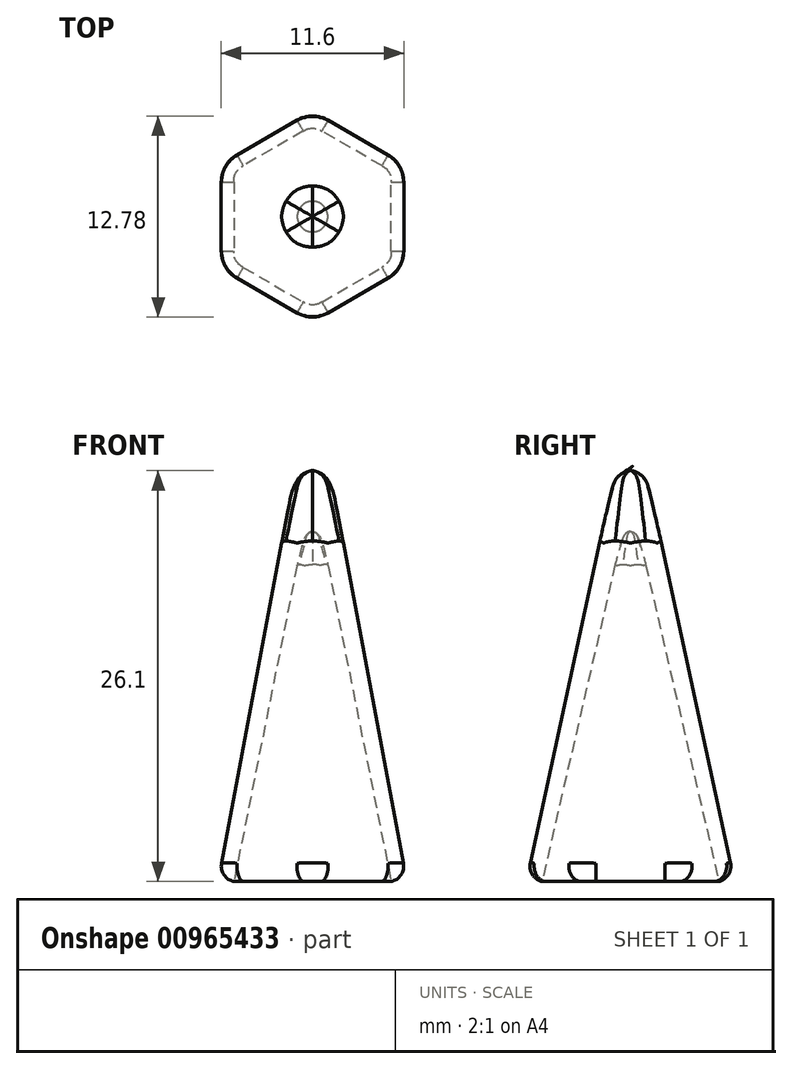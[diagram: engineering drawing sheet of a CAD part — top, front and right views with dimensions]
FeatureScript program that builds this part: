
annotation { "Feature Type Name" : "Feature", "Feature Type Description" : "" }
export const myFeature = defineFeature(function(context is Context, id is Id, definition is map)
    precondition{}
    {
        {
            var Q0;
            Q0=qCreatedBy(makeId("Top.planeOp"),FACE);
            var sketch = newSketch(context, id + "F0", { "sketchPlane" : qUnion([Q0])});
            skPoint(sketch, "E0", {"position": v(0, 5.77) * mm});
            skPoint(sketch, "E1.1.0", {"position": v(-5, 2.89) * mm});
            skPoint(sketch, "E1.2.0", {"position": v(-5, -2.89) * mm});
            skPoint(sketch, "E1.3.0", {"position": v(0, -5.77) * mm});
            skPoint(sketch, "E1.4.0", {"position": v(5, -2.89) * mm});
            skPoint(sketch, "E1.5.0", {"position": v(5, 2.89) * mm});
            skPoint(sketch, "E1.center", {"position": v(0, 0) * mm});
            skLineSegment(sketch, "E2", {"start": v(0, 5.77) * mm, "end": v(5, 2.89) * mm});
            skLineSegment(sketch, "E3", {"start": v(5, -2.89) * mm, "end": v(0, -5.77) * mm});
            skLineSegment(sketch, "E4", {"start": v(-5, -2.89) * mm, "end": v(-5, 2.89) * mm});
            skLineSegment(sketch, "E5", {"start": v(-5, 2.89) * mm, "end": v(0, 5.77) * mm});
            skLineSegment(sketch, "E6", {"start": v(5, 2.89) * mm, "end": v(5, -2.89) * mm});
            skLineSegment(sketch, "E7", {"start": v(0, -5.77) * mm, "end": v(-5, -2.89) * mm});
            skLineSegment(sketch, "E8.0", {"start": v(0, -6.93) * mm, "end": v(-6, -3.46) * mm});
            skLineSegment(sketch, "E8.1", {"start": v(-6, 3.46) * mm, "end": v(0, 6.93) * mm});
            skLineSegment(sketch, "E8.2", {"start": v(0, 6.93) * mm, "end": v(6, 3.46) * mm});
            skLineSegment(sketch, "E8.3", {"start": v(-6, -3.46) * mm, "end": v(-6, 3.46) * mm});
            skLineSegment(sketch, "E8.4", {"start": v(6, 3.46) * mm, "end": v(6, -3.46) * mm});
            skLineSegment(sketch, "E8.5", {"start": v(6, -3.46) * mm, "end": v(0, -6.93) * mm});
            skSolve(sketch);
        }
        {
            var Q0;
            Q0=qCreatedBy(makeId("Top.planeOp"),FACE);
            cPlane(context, id + "F1", {"entities" : qUnion([Q0]), "cplaneType" : CPlaneType.OFFSET, "offset" : 25 * mm, "width" : 150 * mm, "height" : 150 * mm});
        }
        {
            var Q0;
            Q0=qCreatedBy(id+"F1.planeOp",FACE);
            var sketch = newSketch(context, id + "F2", { "sketchPlane" : qUnion([Q0])});
            skPoint(sketch, "E9", {"position": v(0, 0) * mm});
            skSolve(sketch);
        }
        {
            var Q0;
            Q0=qCreatedBy(makeId("Top.planeOp"),FACE);
            cPlane(context, id + "F3", {"entities" : qUnion([Q0]), "cplaneType" : CPlaneType.OFFSET, "offset" : 32 * mm, "width" : 150 * mm, "height" : 150 * mm});
        }
        {
            var Q0;
            Q0=qCreatedBy(id+"F3.planeOp",FACE);
            var sketch = newSketch(context, id + "F4", { "sketchPlane" : qUnion([Q0])});
            skPoint(sketch, "E10", {"position": v(0, 0) * mm});
            skSolve(sketch);
        }
        {
            var Q0;
            Q0=qCreatedBy(makeId("Top.planeOp"),FACE);
            var sketch = newSketch(context, id + "F5", { "sketchPlane" : qUnion([Q0])});
            skPoint(sketch, "E11", {"position": v(0, 6.93) * mm});
            skPoint(sketch, "E12.1.0", {"position": v(-6, 3.46) * mm});
            skPoint(sketch, "E12.2.0", {"position": v(-6, -3.46) * mm});
            skPoint(sketch, "E12.3.0", {"position": v(0, -6.93) * mm});
            skPoint(sketch, "E12.4.0", {"position": v(6, -3.46) * mm});
            skPoint(sketch, "E12.5.0", {"position": v(6, 3.46) * mm});
            skPoint(sketch, "E12.center", {"position": v(0, 0) * mm});
            skLineSegment(sketch, "E13", {"start": v(-6, 3.46) * mm, "end": v(0, 6.93) * mm});
            skLineSegment(sketch, "E14", {"start": v(0, 6.93) * mm, "end": v(6, 3.46) * mm});
            skLineSegment(sketch, "E15", {"start": v(6, 3.46) * mm, "end": v(6, -3.46) * mm});
            skLineSegment(sketch, "E16", {"start": v(6, -3.46) * mm, "end": v(0, -6.93) * mm});
            skLineSegment(sketch, "E17", {"start": v(0, -6.93) * mm, "end": v(-6, -3.46) * mm});
            skLineSegment(sketch, "E18", {"start": v(-6, -3.46) * mm, "end": v(-6, 3.46) * mm});
            skSolve(sketch);
        }
        {
            var Q0;
            Q0=makeQuery(id+"F5.imprint","IMPRINT",FACE,{"disambiguationData":[TD([[makeQuery(id+"F5.imprint","IMPRINT",EDGE,{"derivedFrom":sQuery(id+"F5.wireOp",EDGE,"E13")}),-1.0]])]});
            var Q1;
            Q1=sQuery(id+"F4.wireOp",VERTEX,"E10");
            loft(context, id + "F6", {"sheetProfilesArray" : [{ "sheetProfileEntities" : qUnion([Q0]) }, { "sheetProfileEntities" : qUnion([Q1]) }]});
        }
        {
            var Q1;
            Q1=makeQuery(id+"F0.imprint","IMPRINT",FACE,{"disambiguationData":[TD([[makeQuery(id+"F0.imprint","IMPRINT",EDGE,{"derivedFrom":sQuery(id+"F0.wireOp",EDGE,"E2")}),-1.0]])]});
            var Q2;
            Q2=sQuery(id+"F2.wireOp",VERTEX,"E9");
            loft(context, id + "F7", {"operationType" : NewBodyOperationType.REMOVE, "sheetProfilesArray" : [{ "sheetProfileEntities" : qUnion([Q1]) }, { "sheetProfileEntities" : qUnion([Q2]) }]});
        }
        {
            var Q0;
            Q0=makeQuery(id+"F6.opLoft","SWEPT_EDGE",EDGE,{"disambiguationData":[OSD([sQuery(id+"F4.wireOp",VERTEX,"E10"),sQuery(id+"F5.wireOp",EDGE,"E14"),sQuery(id+"F5.wireOp",EDGE,"E15")])]});
            var Q1;
            Q1=makeQuery(id+"F6.opLoft","SWEPT_EDGE",EDGE,{"disambiguationData":[OSD([sQuery(id+"F4.wireOp",VERTEX,"E10"),sQuery(id+"F5.wireOp",EDGE,"E15"),sQuery(id+"F5.wireOp",EDGE,"E16")])]});
            var Q2;
            Q2=makeQuery(id+"F6.opLoft","SWEPT_EDGE",EDGE,{"disambiguationData":[OSD([sQuery(id+"F4.wireOp",VERTEX,"E10"),sQuery(id+"F5.wireOp",EDGE,"E16"),sQuery(id+"F5.wireOp",EDGE,"E17")])]});
            var Q3;
            Q3=makeQuery(id+"F6.opLoft","SWEPT_EDGE",EDGE,{"disambiguationData":[OSD([sQuery(id+"F4.wireOp",VERTEX,"E10"),sQuery(id+"F5.wireOp",EDGE,"E17"),sQuery(id+"F5.wireOp",EDGE,"E18")])]});
            var Q4;
            Q4=makeQuery(id+"F6.opLoft","SWEPT_EDGE",EDGE,{"disambiguationData":[OSD([sQuery(id+"F4.wireOp",VERTEX,"E10"),sQuery(id+"F5.wireOp",EDGE,"E13"),sQuery(id+"F5.wireOp",EDGE,"E18")])]});
            var Q5;
            Q5=makeQuery(id+"F6.opLoft","SWEPT_EDGE",EDGE,{"disambiguationData":[OSD([sQuery(id+"F4.wireOp",VERTEX,"E10"),sQuery(id+"F5.wireOp",EDGE,"E13"),sQuery(id+"F5.wireOp",EDGE,"E14")])]});
            fillet(context, id + "F8", {"entities" : qUnion([Q0, Q1, Q2, Q3, Q4, Q5]), "radius" : 2 * mm, "tangentPropagation" : true, "allowEdgeOverflow" : false});
        }
        {
            var Q0;
            Q0=makeQuery(id+"F7.boolean.opBoolean","COPY",EDGE,{"derivedFrom":makeQuery(id+"F7.opLoft","SWEPT_EDGE",EDGE,{"disambiguationData":[OSD([sQuery(id+"F0.wireOp",EDGE,"E4"),sQuery(id+"F0.wireOp",EDGE,"E7"),sQuery(id+"F2.wireOp",VERTEX,"E9")])]})});
            var Q1;
            Q1=makeQuery(id+"F7.boolean.opBoolean","COPY",EDGE,{"derivedFrom":makeQuery(id+"F7.opLoft","SWEPT_EDGE",EDGE,{"disambiguationData":[OSD([sQuery(id+"F0.wireOp",EDGE,"E3"),sQuery(id+"F0.wireOp",EDGE,"E7"),sQuery(id+"F2.wireOp",VERTEX,"E9")])]})});
            var Q2;
            Q2=makeQuery(id+"F7.boolean.opBoolean","COPY",EDGE,{"derivedFrom":makeQuery(id+"F7.opLoft","SWEPT_EDGE",EDGE,{"disambiguationData":[OSD([sQuery(id+"F0.wireOp",EDGE,"E3"),sQuery(id+"F0.wireOp",EDGE,"E6"),sQuery(id+"F2.wireOp",VERTEX,"E9")])]})});
            var Q3;
            Q3=makeQuery(id+"F7.boolean.opBoolean","COPY",EDGE,{"derivedFrom":makeQuery(id+"F7.opLoft","SWEPT_EDGE",EDGE,{"disambiguationData":[OSD([sQuery(id+"F0.wireOp",EDGE,"E2"),sQuery(id+"F0.wireOp",EDGE,"E6"),sQuery(id+"F2.wireOp",VERTEX,"E9")])]})});
            var Q4;
            Q4=makeQuery(id+"F7.boolean.opBoolean","COPY",EDGE,{"derivedFrom":makeQuery(id+"F7.opLoft","SWEPT_EDGE",EDGE,{"disambiguationData":[OSD([sQuery(id+"F0.wireOp",EDGE,"E2"),sQuery(id+"F0.wireOp",EDGE,"E5"),sQuery(id+"F2.wireOp",VERTEX,"E9")])]})});
            var Q5;
            Q5=makeQuery(id+"F7.boolean.opBoolean","COPY",EDGE,{"derivedFrom":makeQuery(id+"F7.opLoft","SWEPT_EDGE",EDGE,{"disambiguationData":[OSD([sQuery(id+"F0.wireOp",EDGE,"E4"),sQuery(id+"F0.wireOp",EDGE,"E5"),sQuery(id+"F2.wireOp",VERTEX,"E9")])]})});
            fillet(context, id + "F9", {"entities" : qUnion([Q0, Q1, Q2, Q3, Q4, Q5]), "radius" : 1 * mm, "tangentPropagation" : true, "allowEdgeOverflow" : false});
        }
        {
            var Q0;
            Q0=makeQuery(id+"F6.opLoft","MID_CAP_EDGE",EDGE,{"disambiguationData":[OSD([sQuery(id+"F5.wireOp",EDGE,"E16"),sQuery(id+"F5.wireOp",EDGE,"E17"),sQuery(id+"F5.wireOp",EDGE,"E18")])],"capPos":0.0});
            var Q1;
            {var subQ0=sQuery(id+"F5.wireOp",EDGE,"E16");var subQ1=sQuery(id+"F5.wireOp",EDGE,"E17");Q1=makeQuery(id+"F8.opFillet","BLEND_EDGE",EDGE,{"blendedFrom":[makeQuery(id+"F6.opLoft","SWEPT_EDGE",EDGE,{"disambiguationData":[OSD([sQuery(id+"F4.wireOp",VERTEX,"E10"),subQ0,subQ1])]}),makeQuery(id+"F6.opLoft","CAP_FACE",FACE,{"disambiguationData":[OSD([makeQuery(id+"F5.imprint","IMPRINT",FACE,{"disambiguationData":[TD([[makeQuery(id+"F5.imprint","IMPRINT",EDGE,{"derivedFrom":sQuery(id+"F5.wireOp",EDGE,"E13")}),-1.0]])]})])],"isStart":true})],"blendedInto":[makeQuery(id+"F6.opLoft","CAP_FACE",FACE,{"disambiguationData":[OSD([makeQuery(id+"F5.imprint","IMPRINT",FACE,{"disambiguationData":[TD([[makeQuery(id+"F5.imprint","IMPRINT",EDGE,{"derivedFrom":sQuery(id+"F5.wireOp",EDGE,"E13")}),-1.0]])]})])],"isStart":true})]});}
            var Q2;
            Q2=makeQuery(id+"F6.opLoft","MID_CAP_EDGE",EDGE,{"disambiguationData":[OSD([sQuery(id+"F5.wireOp",EDGE,"E15"),sQuery(id+"F5.wireOp",EDGE,"E16"),sQuery(id+"F5.wireOp",EDGE,"E17")])],"capPos":0.0});
            var Q3;
            {var subQ0=sQuery(id+"F5.wireOp",EDGE,"E16");var subQ1=sQuery(id+"F5.wireOp",EDGE,"E15");Q3=makeQuery(id+"F8.opFillet","BLEND_EDGE",EDGE,{"blendedFrom":[makeQuery(id+"F6.opLoft","SWEPT_EDGE",EDGE,{"disambiguationData":[OSD([sQuery(id+"F4.wireOp",VERTEX,"E10"),subQ1,subQ0])]}),makeQuery(id+"F6.opLoft","CAP_FACE",FACE,{"disambiguationData":[OSD([makeQuery(id+"F5.imprint","IMPRINT",FACE,{"disambiguationData":[TD([[makeQuery(id+"F5.imprint","IMPRINT",EDGE,{"derivedFrom":sQuery(id+"F5.wireOp",EDGE,"E13")}),-1.0]])]})])],"isStart":true})],"blendedInto":[makeQuery(id+"F6.opLoft","CAP_FACE",FACE,{"disambiguationData":[OSD([makeQuery(id+"F5.imprint","IMPRINT",FACE,{"disambiguationData":[TD([[makeQuery(id+"F5.imprint","IMPRINT",EDGE,{"derivedFrom":sQuery(id+"F5.wireOp",EDGE,"E13")}),-1.0]])]})])],"isStart":true})]});}
            var Q4;
            Q4=makeQuery(id+"F6.opLoft","MID_CAP_EDGE",EDGE,{"disambiguationData":[OSD([sQuery(id+"F5.wireOp",EDGE,"E14"),sQuery(id+"F5.wireOp",EDGE,"E15"),sQuery(id+"F5.wireOp",EDGE,"E16")])],"capPos":0.0});
            var Q5;
            {var subQ0=sQuery(id+"F5.wireOp",EDGE,"E15");var subQ1=sQuery(id+"F5.wireOp",EDGE,"E14");Q5=makeQuery(id+"F8.opFillet","BLEND_EDGE",EDGE,{"blendedFrom":[makeQuery(id+"F6.opLoft","SWEPT_EDGE",EDGE,{"disambiguationData":[OSD([sQuery(id+"F4.wireOp",VERTEX,"E10"),subQ1,subQ0])]}),makeQuery(id+"F6.opLoft","CAP_FACE",FACE,{"disambiguationData":[OSD([makeQuery(id+"F5.imprint","IMPRINT",FACE,{"disambiguationData":[TD([[makeQuery(id+"F5.imprint","IMPRINT",EDGE,{"derivedFrom":sQuery(id+"F5.wireOp",EDGE,"E13")}),-1.0]])]})])],"isStart":true})],"blendedInto":[makeQuery(id+"F6.opLoft","CAP_FACE",FACE,{"disambiguationData":[OSD([makeQuery(id+"F5.imprint","IMPRINT",FACE,{"disambiguationData":[TD([[makeQuery(id+"F5.imprint","IMPRINT",EDGE,{"derivedFrom":sQuery(id+"F5.wireOp",EDGE,"E13")}),-1.0]])]})])],"isStart":true})]});}
            var Q6;
            Q6=makeQuery(id+"F6.opLoft","MID_CAP_EDGE",EDGE,{"disambiguationData":[OSD([sQuery(id+"F5.wireOp",EDGE,"E13"),sQuery(id+"F5.wireOp",EDGE,"E14"),sQuery(id+"F5.wireOp",EDGE,"E15")])],"capPos":0.0});
            var Q7;
            {var subQ0=sQuery(id+"F5.wireOp",EDGE,"E14");var subQ1=sQuery(id+"F5.wireOp",EDGE,"E13");Q7=makeQuery(id+"F8.opFillet","BLEND_EDGE",EDGE,{"blendedFrom":[makeQuery(id+"F6.opLoft","SWEPT_EDGE",EDGE,{"disambiguationData":[OSD([sQuery(id+"F4.wireOp",VERTEX,"E10"),subQ1,subQ0])]}),makeQuery(id+"F6.opLoft","CAP_FACE",FACE,{"disambiguationData":[OSD([makeQuery(id+"F5.imprint","IMPRINT",FACE,{"disambiguationData":[TD([[makeQuery(id+"F5.imprint","IMPRINT",EDGE,{"derivedFrom":subQ1}),-1.0]])]})])],"isStart":true})],"blendedInto":[makeQuery(id+"F6.opLoft","CAP_FACE",FACE,{"disambiguationData":[OSD([makeQuery(id+"F5.imprint","IMPRINT",FACE,{"disambiguationData":[TD([[makeQuery(id+"F5.imprint","IMPRINT",EDGE,{"derivedFrom":subQ1}),-1.0]])]})])],"isStart":true})]});}
            var Q8;
            Q8=makeQuery(id+"F6.opLoft","MID_CAP_EDGE",EDGE,{"disambiguationData":[OSD([sQuery(id+"F5.wireOp",EDGE,"E13"),sQuery(id+"F5.wireOp",EDGE,"E14"),sQuery(id+"F5.wireOp",EDGE,"E18")])],"capPos":0.0});
            var Q9;
            {var subQ0=sQuery(id+"F5.wireOp",EDGE,"E13");var subQ1=sQuery(id+"F5.wireOp",EDGE,"E18");Q9=makeQuery(id+"F8.opFillet","BLEND_EDGE",EDGE,{"blendedFrom":[makeQuery(id+"F6.opLoft","SWEPT_EDGE",EDGE,{"disambiguationData":[OSD([sQuery(id+"F4.wireOp",VERTEX,"E10"),subQ0,subQ1])]}),makeQuery(id+"F6.opLoft","CAP_FACE",FACE,{"disambiguationData":[OSD([makeQuery(id+"F5.imprint","IMPRINT",FACE,{"disambiguationData":[TD([[makeQuery(id+"F5.imprint","IMPRINT",EDGE,{"derivedFrom":subQ0}),-1.0]])]})])],"isStart":true})],"blendedInto":[makeQuery(id+"F6.opLoft","CAP_FACE",FACE,{"disambiguationData":[OSD([makeQuery(id+"F5.imprint","IMPRINT",FACE,{"disambiguationData":[TD([[makeQuery(id+"F5.imprint","IMPRINT",EDGE,{"derivedFrom":subQ0}),-1.0]])]})])],"isStart":true})]});}
            var Q10;
            Q10=makeQuery(id+"F6.opLoft","MID_CAP_EDGE",EDGE,{"disambiguationData":[OSD([sQuery(id+"F5.wireOp",EDGE,"E13"),sQuery(id+"F5.wireOp",EDGE,"E17"),sQuery(id+"F5.wireOp",EDGE,"E18")])],"capPos":0.0});
            var Q11;
            {var subQ0=sQuery(id+"F5.wireOp",EDGE,"E17");var subQ1=sQuery(id+"F5.wireOp",EDGE,"E18");Q11=makeQuery(id+"F8.opFillet","BLEND_EDGE",EDGE,{"blendedFrom":[makeQuery(id+"F6.opLoft","SWEPT_EDGE",EDGE,{"disambiguationData":[OSD([sQuery(id+"F4.wireOp",VERTEX,"E10"),subQ0,subQ1])]}),makeQuery(id+"F6.opLoft","CAP_FACE",FACE,{"disambiguationData":[OSD([makeQuery(id+"F5.imprint","IMPRINT",FACE,{"disambiguationData":[TD([[makeQuery(id+"F5.imprint","IMPRINT",EDGE,{"derivedFrom":sQuery(id+"F5.wireOp",EDGE,"E13")}),-1.0]])]})])],"isStart":true})],"blendedInto":[makeQuery(id+"F6.opLoft","CAP_FACE",FACE,{"disambiguationData":[OSD([makeQuery(id+"F5.imprint","IMPRINT",FACE,{"disambiguationData":[TD([[makeQuery(id+"F5.imprint","IMPRINT",EDGE,{"derivedFrom":sQuery(id+"F5.wireOp",EDGE,"E13")}),-1.0]])]})])],"isStart":true})]});}
            fillet(context, id + "F10", {"entities" : qUnion([Q0, Q1, Q2, Q3, Q4, Q5, Q6, Q7, Q8, Q9, Q10, Q11]), "radius" : 1 * mm, "tangentPropagation" : true, "allowEdgeOverflow" : false});
        }
    });
